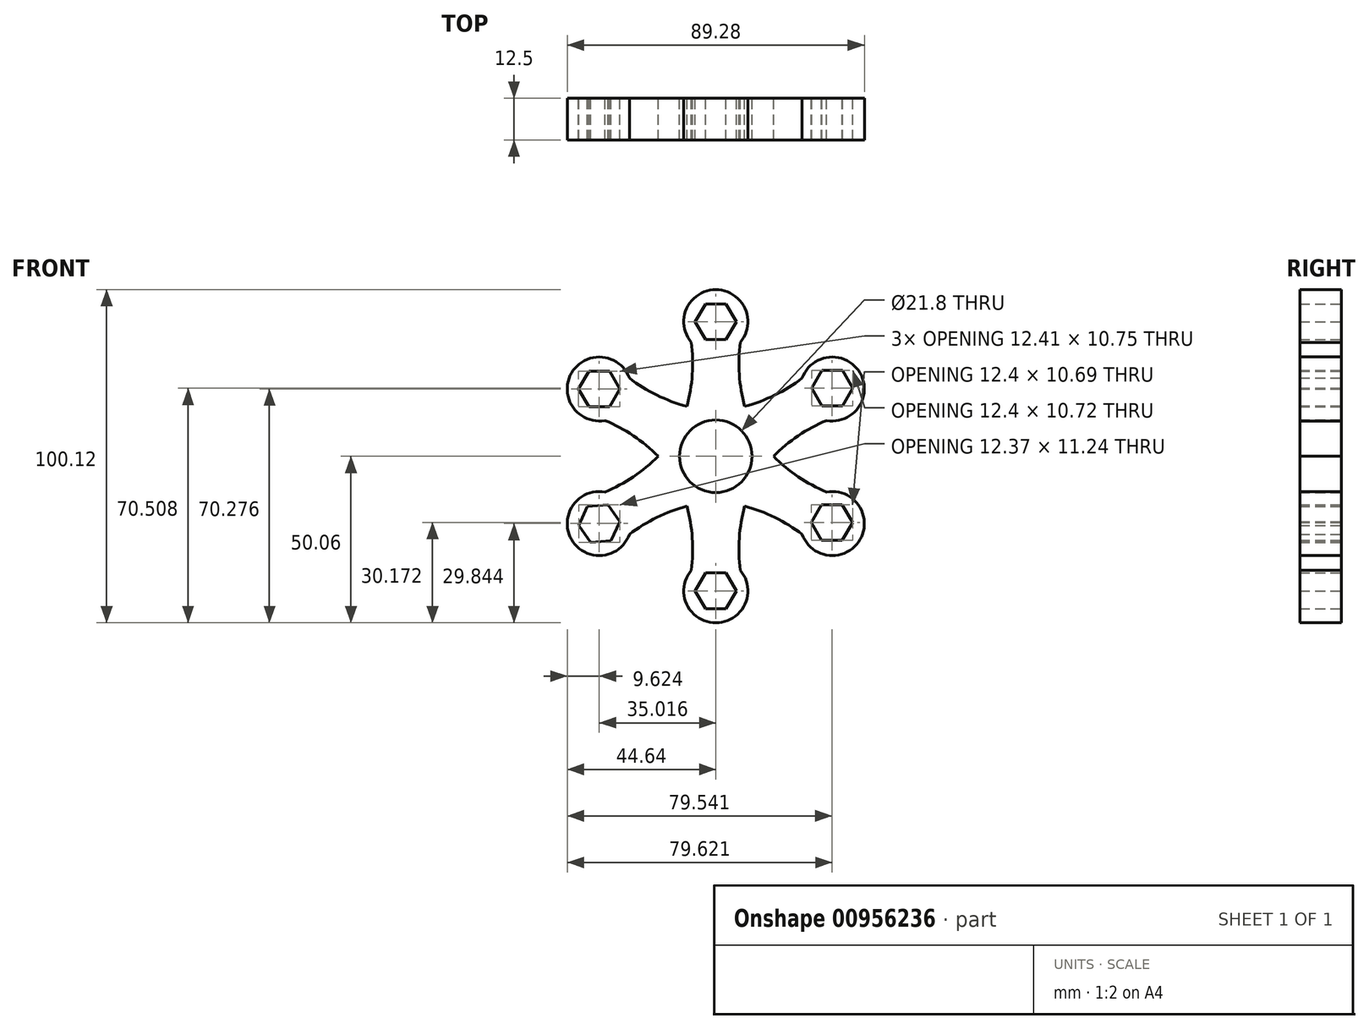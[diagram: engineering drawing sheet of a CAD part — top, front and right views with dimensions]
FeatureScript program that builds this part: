
annotation { "Feature Type Name" : "Feature", "Feature Type Description" : "" }
export const myFeature = defineFeature(function(context is Context, id is Id, definition is map)
    precondition{}
    {
        {
            var Q0;
            Q0=qCreatedBy(makeId("Front.planeOp"),FACE);
            var sketch = newSketch(context, id + "F0", { "sketchPlane" : qUnion([Q0])});
            skArc(sketch, "E0", {"start": v(7.35, 34.22) * mm, "mid": v(7.06, 24.55) * mm, "end": v(8.67, 15.01) * mm});
            skArc(sketch, "E1", {"start": v(7.35, 34.22) * mm, "mid": v(0, 50.06) * mm, "end": v(-7.35, 34.22) * mm});
            skArc(sketch, "E2.MirrorCS", {"start": v(-7.35, 34.22) * mm, "mid": v(-7.06, 24.55) * mm, "end": v(-8.67, 15.01) * mm});
            skPoint(sketch, "E3.orphan", {"position": v(-13.92, 2.7) * mm});
            skPoint(sketch, "E4.orphan", {"position": v(13.92, 2.7) * mm});
            skPoint(sketch, "E5.start.orphan", {"position": v(0, 57.12) * mm});
            skArc(sketch, "E6.1.0", {"start": v(-25.96, 23.48) * mm, "mid": v(-43.35, 25.03) * mm, "end": v(-33.31, 10.74) * mm});
            skArc(sketch, "E6.1.1", {"start": v(-33.31, 10.74) * mm, "mid": v(-24.79, 6.16) * mm, "end": v(-17.33, 0) * mm});
            skArc(sketch, "E6.1.2", {"start": v(-25.96, 23.48) * mm, "mid": v(-17.73, 18.38) * mm, "end": v(-8.67, 15.01) * mm});
            skArc(sketch, "E6.2.0", {"start": v(-33.31, -10.74) * mm, "mid": v(-43.35, -25.03) * mm, "end": v(-25.96, -23.48) * mm});
            skArc(sketch, "E6.2.1", {"start": v(-25.96, -23.48) * mm, "mid": v(-17.73, -18.38) * mm, "end": v(-8.67, -15.01) * mm});
            skArc(sketch, "E6.2.2", {"start": v(-33.31, -10.74) * mm, "mid": v(-24.79, -6.16) * mm, "end": v(-17.33, 0) * mm});
            skPoint(sketch, "E6.center", {"position": v(0, 0) * mm});
            skCircle(sketch, "E7", {"center": v(0, 0) * mm, "radius": 10.9 * mm});
            skArc(sketch, "E8.4.3.0", {"start": v(7.35, -34.22) * mm, "mid": v(7.06, -24.55) * mm, "end": v(8.67, -15.01) * mm});
            skArc(sketch, "E8.5.3.0", {"start": v(-7.35, -34.22) * mm, "mid": v(0, -50.06) * mm, "end": v(7.35, -34.22) * mm});
            skArc(sketch, "E8.8.3.0", {"start": v(-7.35, -34.22) * mm, "mid": v(-7.06, -24.55) * mm, "end": v(-8.67, -15.01) * mm});
            skArc(sketch, "E9.4.4.0", {"start": v(33.31, -10.74) * mm, "mid": v(24.79, -6.16) * mm, "end": v(17.33, 0) * mm});
            skArc(sketch, "E9.5.4.0", {"start": v(25.96, -23.48) * mm, "mid": v(43.35, -25.03) * mm, "end": v(33.31, -10.74) * mm});
            skArc(sketch, "E9.8.4.0", {"start": v(25.96, -23.48) * mm, "mid": v(17.73, -18.38) * mm, "end": v(8.67, -15.01) * mm});
            skArc(sketch, "E10.4.5.0", {"start": v(25.96, 23.48) * mm, "mid": v(17.73, 18.38) * mm, "end": v(8.67, 15.01) * mm});
            skArc(sketch, "E10.5.5.0", {"start": v(33.31, 10.74) * mm, "mid": v(43.35, 25.03) * mm, "end": v(25.96, 23.48) * mm});
            skArc(sketch, "E10.8.5.0", {"start": v(33.31, 10.74) * mm, "mid": v(24.79, 6.16) * mm, "end": v(17.33, 0) * mm});
            skPoint(sketch, "E11.orphan", {"position": v(-10.53, 9.5) * mm});
            skPoint(sketch, "E12.orphan", {"position": v(-2.95, 13.87) * mm});
            skPoint(sketch, "E13.orphan", {"position": v(-13.48, 4.37) * mm});
            skPoint(sketch, "E14.orphan", {"position": v(-13.48, -4.37) * mm});
            skPoint(sketch, "E15.orphan", {"position": v(-10.53, -9.5) * mm});
            skPoint(sketch, "E16.orphan", {"position": v(-2.95, -13.87) * mm});
            skPoint(sketch, "E17.orphan", {"position": v(2.95, -13.87) * mm});
            skPoint(sketch, "E18.orphan", {"position": v(10.53, -9.5) * mm});
            skPoint(sketch, "E19.orphan", {"position": v(13.48, -4.37) * mm});
            skPoint(sketch, "E20.orphan", {"position": v(13.48, 4.37) * mm});
            skPoint(sketch, "E21.orphan", {"position": v(2.95, 13.87) * mm});
            skPoint(sketch, "E22.orphan", {"position": v(10.53, 9.5) * mm});
            skCircle(sketch, "E23.cCircle", {"center": v(0, 40.43) * mm, "radius": 5.37 * mm, "construction": true});
            skLineSegment(sketch, "E23.0", {"start": v(-3.1, 45.8) * mm, "end": v(3.1, 45.8) * mm});
            skLineSegment(sketch, "E23.1", {"start": v(3.1, 45.8) * mm, "end": v(6.2, 40.43) * mm});
            skLineSegment(sketch, "E23.2", {"start": v(6.2, 40.43) * mm, "end": v(3.1, 35.06) * mm});
            skLineSegment(sketch, "E23.3", {"start": v(3.1, 35.06) * mm, "end": v(-3.1, 35.06) * mm});
            skLineSegment(sketch, "E23.4", {"start": v(-3.1, 35.06) * mm, "end": v(-6.2, 40.43) * mm});
            skLineSegment(sketch, "E23.5", {"start": v(-6.2, 40.43) * mm, "end": v(-3.1, 45.8) * mm});
            skPoint(sketch, "E23.0.midPoint", {"position": v(0, 45.8) * mm});
            skCircle(sketch, "E24.cCircle", {"center": v(-35.02, 20.22) * mm, "radius": 5.37 * mm, "construction": true});
            skLineSegment(sketch, "E24.0", {"start": v(-38.12, 25.6) * mm, "end": v(-31.91, 25.6) * mm});
            skLineSegment(sketch, "E24.1", {"start": v(-31.91, 25.6) * mm, "end": v(-28.8, 20.22) * mm});
            skLineSegment(sketch, "E24.2", {"start": v(-28.8, 20.22) * mm, "end": v(-31.91, 14.84) * mm});
            skLineSegment(sketch, "E24.3", {"start": v(-31.91, 14.84) * mm, "end": v(-38.12, 14.84) * mm});
            skLineSegment(sketch, "E24.4", {"start": v(-38.12, 14.84) * mm, "end": v(-41.22, 20.22) * mm});
            skLineSegment(sketch, "E24.5", {"start": v(-41.22, 20.22) * mm, "end": v(-38.12, 25.6) * mm});
            skPoint(sketch, "E24.0.midPoint", {"position": v(-35.02, 25.6) * mm});
            skCircle(sketch, "E25.cCircle", {"center": v(-35.02, -20.22) * mm, "radius": 5.37 * mm, "construction": true});
            skLineSegment(sketch, "E25.0", {"start": v(-32.38, -14.6) * mm, "end": v(-28.83, -19.7) * mm});
            skLineSegment(sketch, "E25.1", {"start": v(-28.83, -19.7) * mm, "end": v(-31.47, -25.3) * mm});
            skLineSegment(sketch, "E25.2", {"start": v(-31.47, -25.3) * mm, "end": v(-37.65, -25.83) * mm});
            skLineSegment(sketch, "E25.3", {"start": v(-37.65, -25.83) * mm, "end": v(-41.2, -20.74) * mm});
            skLineSegment(sketch, "E25.4", {"start": v(-41.2, -20.74) * mm, "end": v(-38.56, -15.12) * mm});
            skLineSegment(sketch, "E25.5", {"start": v(-38.56, -15.12) * mm, "end": v(-32.38, -14.6) * mm});
            skPoint(sketch, "E25.0.midPoint", {"position": v(-30.6, -17.14) * mm});
            skCircle(sketch, "E26.cCircle", {"center": v(0, -40.43) * mm, "radius": 5.38 * mm, "construction": true});
            skLineSegment(sketch, "E26.0", {"start": v(-3.1, -35.06) * mm, "end": v(3.1, -35.06) * mm});
            skLineSegment(sketch, "E26.1", {"start": v(3.1, -35.06) * mm, "end": v(6.2, -40.43) * mm});
            skLineSegment(sketch, "E26.2", {"start": v(6.2, -40.43) * mm, "end": v(3.1, -45.8) * mm});
            skLineSegment(sketch, "E26.3", {"start": v(3.1, -45.8) * mm, "end": v(-3.1, -45.8) * mm});
            skLineSegment(sketch, "E26.4", {"start": v(-3.1, -45.8) * mm, "end": v(-6.2, -40.43) * mm});
            skLineSegment(sketch, "E26.5", {"start": v(-6.2, -40.43) * mm, "end": v(-3.1, -35.06) * mm});
            skPoint(sketch, "E26.0.midPoint", {"position": v(0, -35.06) * mm});
            skLineSegment(sketch, "E27.0", {"start": v(31.87, 25.78) * mm, "end": v(38.1, 25.8) * mm});
            skLineSegment(sketch, "E27.1", {"start": v(38.1, 25.8) * mm, "end": v(41.18, 20.46) * mm});
            skLineSegment(sketch, "E27.2", {"start": v(41.18, 20.46) * mm, "end": v(38.04, 15.09) * mm});
            skLineSegment(sketch, "E27.3", {"start": v(38.04, 15.09) * mm, "end": v(31.87, 15.09) * mm});
            skLineSegment(sketch, "E27.4", {"start": v(31.87, 15.09) * mm, "end": v(28.78, 20.43) * mm});
            skLineSegment(sketch, "E27.5", {"start": v(28.78, 20.43) * mm, "end": v(31.87, 25.78) * mm});
            skLineSegment(sketch, "E28.0", {"start": v(31.79, -14.54) * mm, "end": v(37.96, -14.54) * mm});
            skLineSegment(sketch, "E28.1", {"start": v(37.96, -14.54) * mm, "end": v(41.1, -19.86) * mm});
            skLineSegment(sketch, "E28.2", {"start": v(41.1, -19.86) * mm, "end": v(37.96, -25.23) * mm});
            skLineSegment(sketch, "E28.3", {"start": v(37.96, -25.23) * mm, "end": v(31.79, -25.23) * mm});
            skLineSegment(sketch, "E28.4", {"start": v(31.79, -25.23) * mm, "end": v(28.7, -19.89) * mm});
            skLineSegment(sketch, "E28.5", {"start": v(28.7, -19.89) * mm, "end": v(31.79, -14.54) * mm});
            skSolve(sketch);
        }
        {
            var Q0;
            Q0=makeQuery(id+"F0.imprint","IMPRINT",FACE,{"disambiguationData":[TD([[makeQuery(id+"F0.imprint","IMPRINT",EDGE,{"derivedFrom":sQuery(id+"F0.wireOp",EDGE,"E0")}),-1.0]])]});
            extrude(context, id + "F1", {"entities" : qUnion([Q0]), "endBound" : BoundingType.SYMMETRIC, "depth" : 12.5 * mm, "offsetDistance" : 25 * mm});
        }
    });
